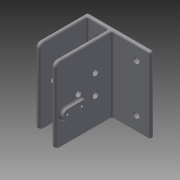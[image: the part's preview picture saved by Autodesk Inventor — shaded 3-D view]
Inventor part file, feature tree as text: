
AUTODESK INVENTOR PART (.ipt)
format: ipt  version: 2014 (Build 180170000, 170)  size: 402,944 bytes
history: native  units: mm
features: extrude x10, sketch x9, fillet x8, projected_geometry x5, other x1
ambient origin geometry x8: Origin, YZ Plane, XZ Plane, XY Plane, X Axis, Y Axis, Z Axis, Center Point
bodies: Body1 (feature_tree)
feature tree (33):
  other  "ソリッド1"
  extrude  "押し出し1"  Depth=4.0mm
  extrude  "押し出し2"  Depth=4.0mm
  fillet  "フィレット1"  Radius=4.0mm
  extrude  "押し出し3"  Depth=60.0mm
  fillet  "フィレット2"  Radius=22.0mm
  fillet  "フィレット3"  Radius=55.0mm
  extrude  "押し出し4"  Depth=80.0mm TaperAngle=0.0deg
  extrude  "押し出し5"  Depth=35.0mm
  fillet  "フィレット4"  Radius=35.0mm
  extrude  "押し出し7"  Depth=22.5mm
  extrude  "押し出し10"  Depth=10.0mm
  fillet  "フィレット7"  Radius=5.0mm
  extrude  "押し出し11"  Depth=17.5mm
  fillet  "フィレット8"  Radius=3.5mm
  extrude  "押し出し12"  Depth=200.0mm TaperAngle=0.0deg
  extrude  "押し出し13"  Depth=5.0mm
  fillet  "フィレット9"  Radius=1.8mm
  fillet  "フィレット10"  Radius=5.0mm
  sketch  "スケッチ1"
  sketch  "スケッチ2"
  sketch  "スケッチ3"
  sketch  "スケッチ5"
  sketch  "スケッチ7"
  projected_geometry  "投影ループ1"
  sketch  "スケッチ10"
  sketch  "スケッチ11"
  sketch  "スケッチ12"
  projected_geometry  "投影ループ2"
  projected_geometry  "投影ループ3"
  projected_geometry  "投影ループ4"
  sketch  "スケッチ13"
  projected_geometry  "投影ループ5"
